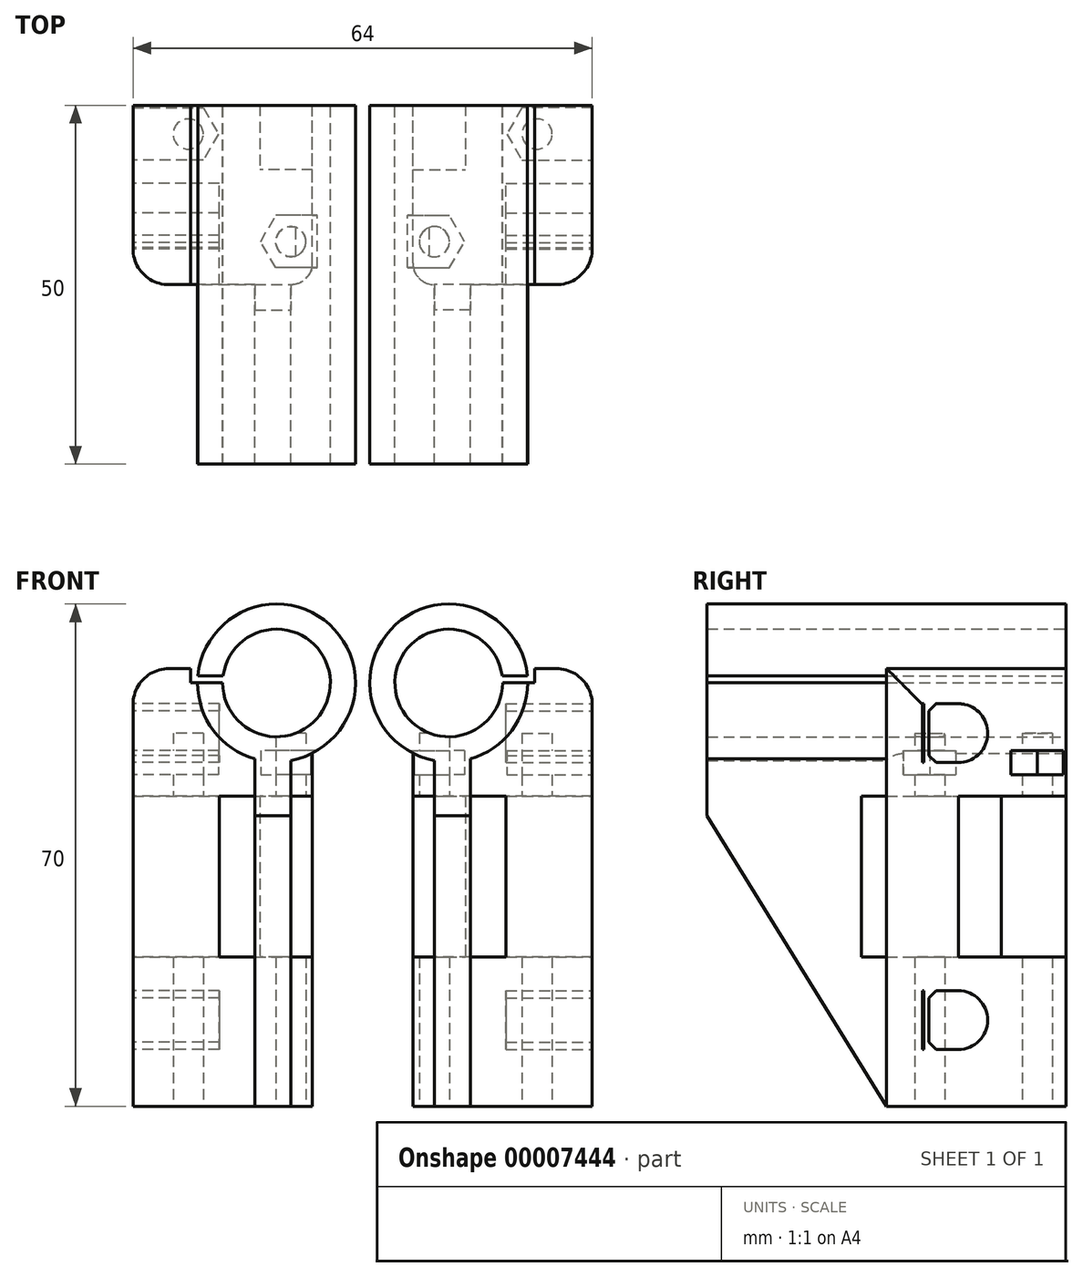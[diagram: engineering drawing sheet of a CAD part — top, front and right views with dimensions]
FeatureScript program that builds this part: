
annotation { "Feature Type Name" : "Feature", "Feature Type Description" : "" }
export const myFeature = defineFeature(function(context is Context, id is Id, definition is map)
    precondition{}
    {
        {
            var Q0;
            Q0=qCreatedBy(makeId("Front.planeOp"),FACE);
            var sketch = newSketch(context, id + "F0", { "sketchPlane" : qUnion([Q0])});
            skCircle(sketch, "E0", {"center": v(12, -12) * mm, "radius": 7.5 * mm});
            skCircle(sketch, "E1", {"center": v(12, -12) * mm, "radius": 11 * mm});
            skLineSegment(sketch, "E2", {"start": v(12, -12) * mm, "end": v(23, -12) * mm});
            skPoint(sketch, "E3.rect.middle", {"position": v(32, -10) * mm});
            skLineSegment(sketch, "E4", {"start": v(32, -10) * mm, "end": v(24, -10) * mm});
            skLineSegment(sketch, "E5", {"start": v(23, -12) * mm, "end": v(24, -12) * mm});
            skLineSegment(sketch, "E6", {"start": v(24, -12) * mm, "end": v(24, -10) * mm});
            skLineSegment(sketch, "E7", {"start": v(12, -12) * mm, "end": v(12, -11) * mm});
            skLineSegment(sketch, "E8", {"start": v(12, -11) * mm, "end": v(22.95, -11) * mm});
            skLineSegment(sketch, "E9", {"start": v(32, -10) * mm, "end": v(32, -71) * mm});
            skLineSegment(sketch, "E10", {"start": v(32, -71) * mm, "end": v(7, -71) * mm});
            skLineSegment(sketch, "E11", {"start": v(7, -71) * mm, "end": v(7, -23) * mm});
            skLineSegment(sketch, "E12", {"start": v(7, -23) * mm, "end": v(12, -23) * mm, "construction": true});
            skLineSegment(sketch, "E13", {"start": v(7, -23) * mm, "end": v(7, -21.8) * mm});
            skSolve(sketch);
        }
        {
            var Q0;
            {var subQ0=sQuery(id+"F0.wireOp",EDGE,"E2");var subQ1=sQuery(id+"F0.wireOp",EDGE,"E0");var subQ2=makeQuery(id+"F0.imprint","INTERSECT",VERTEX,{"derivedFrom":[subQ1,subQ0]});Q0=makeQuery(id+"F0.imprint","IMPRINT",FACE,{"disambiguationData":[TD([[makeQuery(id+"F0.imprint","IMPRINT",EDGE,{"disambiguationData":[TD([[subQ2,1.0]])],"derivedFrom":subQ1}),-1.0]])]});}
            extrude(context, id + "F1", {"entities" : qUnion([Q0]), "depth" : 50 * mm});
        }
        {
            var Q0;
            Q0=makeQuery(id+"F0.imprint","IMPRINT",FACE,{"disambiguationData":[TD([[makeQuery(id+"F0.imprint","IMPRINT",EDGE,{"derivedFrom":sQuery(id+"F0.wireOp",EDGE,"E4")}),1.0]])]});
            extrude(context, id + "F2", {"entities" : qUnion([Q0]), "operationType" : NewBodyOperationType.ADD, "depth" : 25 * mm});
        }
        {
            var Q0;
            Q0=makeQuery(id+"F2.opExtrude","SWEPT_FACE",FACE,{"disambiguationData":[OSD([sQuery(id+"F0.wireOp",EDGE,"E9")])]});
            var sketch = newSketch(context, id + "F3", { "sketchPlane" : qUnion([Q0])});
            skLineSegment(sketch, "E14", {"start": v(0, -71) * mm, "end": v(-15, -71) * mm, "construction": true});
            skLineSegment(sketch, "E15", {"start": v(-15, -71) * mm, "end": v(-15, -59) * mm, "construction": true});
            skLineSegment(sketch, "E16", {"start": v(-15, -59) * mm, "end": v(-15, -19) * mm, "construction": true});
            skCircle(sketch, "E17", {"center": v(-15, -59) * mm, "radius": 4.1 * mm});
            skCircle(sketch, "E18", {"center": v(-15, -59) * mm, "radius": 7.5 * mm, "construction": true});
            skCircle(sketch, "E19", {"center": v(-15, -19) * mm, "radius": 7.5 * mm, "construction": true});
            skLineSegment(sketch, "E20", {"start": v(-15, -39) * mm, "end": v(-16.5, -39) * mm, "construction": true});
            skLineSegment(sketch, "E21", {"start": v(-16.5, -39) * mm, "end": v(-16.5, -44.4) * mm, "construction": true});
            skCircle(sketch, "E22", {"center": v(-16.5, -44.4) * mm, "radius": 3 * mm, "construction": true});
            skCircle(sketch, "E23.0.MirrorC", {"center": v(-16.5, -33.6) * mm, "radius": 3 * mm, "construction": true});
            skLineSegment(sketch, "E24", {"start": v(-15, -54.9) * mm, "end": v(-20, -54.9) * mm, "construction": true});
            skLineSegment(sketch, "E25", {"start": v(-15, -63.1) * mm, "end": v(-20, -63.1) * mm, "construction": true});
            skLineSegment(sketch, "E26", {"start": v(-19.1, -54.9) * mm, "end": v(-19.1, -63.1) * mm});
            skLineSegment(sketch, "E27", {"start": v(-19.1, -55.9) * mm, "end": v(-18.1, -54.9) * mm});
            skLineSegment(sketch, "E28", {"start": v(-18.1, -54.9) * mm, "end": v(-15, -54.9) * mm});
            skLineSegment(sketch, "E29", {"start": v(-15, -63.1) * mm, "end": v(-18.1, -63.1) * mm});
            skLineSegment(sketch, "E30", {"start": v(-18.1, -63.1) * mm, "end": v(-19.1, -62.1) * mm});
            skLineSegment(sketch, "E31.bottom", {"start": v(-19.8, -54.9) * mm, "end": v(-20, -54.9) * mm});
            skLineSegment(sketch, "E31.top", {"start": v(-19.8, -63.1) * mm, "end": v(-20, -63.1) * mm});
            skLineSegment(sketch, "E31.left", {"start": v(-19.8, -54.9) * mm, "end": v(-19.8, -63.1) * mm});
            skLineSegment(sketch, "E31.right", {"start": v(-20, -54.9) * mm, "end": v(-20, -63.1) * mm});
            skLineSegment(sketch, "E32", {"start": v(-15, -39) * mm, "end": v(5.06, -39) * mm, "construction": true});
            skLineSegment(sketch, "E33.MirrorCS", {"start": v(-19.8, -23.1) * mm, "end": v(-20, -23.1) * mm});
            skLineSegment(sketch, "E34.MirrorCS", {"start": v(-19.8, -14.9) * mm, "end": v(-20, -14.9) * mm});
            skLineSegment(sketch, "E35.MirrorCS", {"start": v(-19.1, -22.1) * mm, "end": v(-18.1, -23.1) * mm});
            skLineSegment(sketch, "E36.MirrorCS", {"start": v(-18.1, -14.9) * mm, "end": v(-19.1, -15.9) * mm});
            skLineSegment(sketch, "E37.MirrorCS", {"start": v(-15, -14.9) * mm, "end": v(-20, -14.9) * mm, "construction": true});
            skLineSegment(sketch, "E38.MirrorCS", {"start": v(-15, -23.1) * mm, "end": v(-20, -23.1) * mm, "construction": true});
            skLineSegment(sketch, "E39.MirrorCS", {"start": v(-18.1, -23.1) * mm, "end": v(-15, -23.1) * mm});
            skLineSegment(sketch, "E40.MirrorCS", {"start": v(-19.8, -23.1) * mm, "end": v(-19.8, -14.9) * mm});
            skLineSegment(sketch, "E41.MirrorCS", {"start": v(-20, -23.1) * mm, "end": v(-20, -14.9) * mm});
            skLineSegment(sketch, "E42.MirrorCS", {"start": v(-19.1, -23.1) * mm, "end": v(-19.1, -14.9) * mm});
            skCircle(sketch, "E43.MirrorC", {"center": v(-15, -19) * mm, "radius": 4.1 * mm});
            skLineSegment(sketch, "E44.MirrorCS", {"start": v(-15, -14.9) * mm, "end": v(-18.1, -14.9) * mm});
            skSolve(sketch);
        }
        {
            var Q0;
            Q0=makeQuery(id+"F2.opExtrude","SWEPT_FACE",FACE,{"disambiguationData":[OSD([sQuery(id+"F0.wireOp",EDGE,"E10")])]});
            var sketch = newSketch(context, id + "F4", { "sketchPlane" : qUnion([Q0])});
            skLineSegment(sketch, "E45", {"start": v(0, 0) * mm, "end": v(0, 19) * mm, "construction": true});
            skLineSegment(sketch, "E46", {"start": v(0, 19) * mm, "end": v(10, 19) * mm, "construction": true});
            skLineSegment(sketch, "E47", {"start": v(10, 19) * mm, "end": v(10, 4) * mm, "construction": true});
            skLineSegment(sketch, "E48", {"start": v(10, 4) * mm, "end": v(24.3, 4) * mm, "construction": true});
            skCircle(sketch, "E49", {"center": v(10, 19) * mm, "radius": 2.1 * mm});
            skCircle(sketch, "E50", {"center": v(10, 19) * mm, "radius": 6.5 * mm, "construction": true});
            skCircle(sketch, "E51", {"center": v(24.3, 4) * mm, "radius": 2.1 * mm});
            skCircle(sketch, "E52", {"center": v(24.3, 4) * mm, "radius": 6.5 * mm, "construction": true});
            skLineSegment(sketch, "E53", {"start": v(14.3, 0) * mm, "end": v(14.3, 9) * mm});
            skLineSegment(sketch, "E54", {"start": v(20, 15) * mm, "end": v(32, 15) * mm});
            skLineSegment(sketch, "E55", {"start": v(32, 15) * mm, "end": v(32, 4) * mm});
            skLineSegment(sketch, "E56", {"start": v(24.3, 4) * mm, "end": v(24.3, 0) * mm, "construction": true});
            skLineSegment(sketch, "E57", {"start": v(24.3, 0) * mm, "end": v(14.3, 0) * mm});
            skLineSegment(sketch, "E58", {"start": v(20, 25) * mm, "end": v(20, 15) * mm});
            skLineSegment(sketch, "E59", {"start": v(7, 9) * mm, "end": v(14.3, 9) * mm});
            skLineSegment(sketch, "E60", {"start": v(7, 9) * mm, "end": v(7, 25) * mm});
            skLineSegment(sketch, "E61", {"start": v(7, 25) * mm, "end": v(20, 25) * mm});
            skLineSegment(sketch, "E62", {"start": v(24.3, 0) * mm, "end": v(32, 0) * mm});
            skLineSegment(sketch, "E63", {"start": v(32, 0) * mm, "end": v(32, 4) * mm});
            skLineSegment(sketch, "E64", {"start": v(32, 4) * mm, "end": v(24.3, 4) * mm, "construction": true});
            skSolve(sketch);
        }
        {
            var Q0;
            Q0=makeQuery(id+"F4.imprint","IMPRINT",FACE,{"disambiguationData":[TD([[makeQuery(id+"F4.imprint","IMPRINT",EDGE,{"derivedFrom":sQuery(id+"F4.wireOp",EDGE,"E49")}),-1.0]])]});
            extrude(context, id + "F5", {"entities" : qUnion([Q0]), "operationType" : NewBodyOperationType.REMOVE, "oppositeDirection" : true, "depth" : 12 * mm + (40 * mm + 22.4 * mm) * .5});
        }
        {
            var Q0;
            Q0=makeQuery(id+"F4.imprint","IMPRINT",FACE,{"disambiguationData":[TD([[makeQuery(id+"F4.imprint","IMPRINT",EDGE,{"derivedFrom":sQuery(id+"F4.wireOp",EDGE,"E49")}),-1.0]])]});
            extrude(context, id + "F6", {"entities" : qUnion([Q0]), "operationType" : NewBodyOperationType.ADD, "oppositeDirection" : true, "depth" : 12 * mm + (40 * mm - 22.4 * mm) * .5});
        }
        {
            var Q0;
            Q0=makeQuery(id+"F4.imprint","IMPRINT",FACE,{"disambiguationData":[TD([[makeQuery(id+"F4.imprint","IMPRINT",EDGE,{"derivedFrom":sQuery(id+"F4.wireOp",EDGE,"E49")}),1.0]])]});
            var Q1;
            Q1=makeQuery(id+"F4.imprint","IMPRINT",FACE,{"disambiguationData":[TD([[makeQuery(id+"F4.imprint","IMPRINT",EDGE,{"derivedFrom":sQuery(id+"F4.wireOp",EDGE,"E51")}),1.0]])]});
            extrude(context, id + "F7", {"entities" : qUnion([Q0, Q1]), "operationType" : NewBodyOperationType.REMOVE, "oppositeDirection" : true, "depth" : 12 * mm + 40 * mm});
        }
        {
            var Q0;
            Q0=makeQuery(id+"F5.boolean.opBoolean","COPY",FACE,{"derivedFrom":makeQuery(id+"F5.opExtrude","CAP_FACE",FACE,{"disambiguationData":[OSD([sQuery(id+"F4.wireOp",EDGE,"E49"),sQuery(id+"F4.wireOp",EDGE,"E51"),sQuery(id+"F4.wireOp",EDGE,"E53"),sQuery(id+"F4.wireOp",EDGE,"E54"),sQuery(id+"F4.wireOp",EDGE,"E55"),sQuery(id+"F4.wireOp",EDGE,"E57"),sQuery(id+"F4.wireOp",EDGE,"E58"),sQuery(id+"F4.wireOp",EDGE,"E59"),sQuery(id+"F4.wireOp",EDGE,"E60"),sQuery(id+"F4.wireOp",EDGE,"E61"),sQuery(id+"F4.wireOp",EDGE,"E62"),sQuery(id+"F4.wireOp",EDGE,"E63")])],"isStart":false})});
            var sketch = newSketch(context, id + "F8", { "sketchPlane" : qUnion([Q0])});
            skCircle(sketch, "E65.cCircle", {"center": v(24.3, 4) * mm, "radius": 3.65 * mm, "construction": true});
            skLineSegment(sketch, "E65.0", {"start": v(28.51, 4) * mm, "end": v(26.4, 0.35) * mm, "construction": true});
            skLineSegment(sketch, "E65.1", {"start": v(26.4, 0.35) * mm, "end": v(22.2, 0.35) * mm});
            skLineSegment(sketch, "E65.2", {"start": v(22.2, 0.35) * mm, "end": v(20.09, 4) * mm});
            skLineSegment(sketch, "E65.3", {"start": v(20.09, 4) * mm, "end": v(22.2, 7.65) * mm});
            skLineSegment(sketch, "E65.4", {"start": v(22.2, 7.65) * mm, "end": v(26.4, 7.65) * mm});
            skLineSegment(sketch, "E65.5", {"start": v(26.4, 7.65) * mm, "end": v(28.51, 4) * mm, "construction": true});
            skPoint(sketch, "E65.0.midPoint", {"position": v(27.46, 2.18) * mm});
            skCircle(sketch, "E66.cCircle", {"center": v(10, 19) * mm, "radius": 3.65 * mm, "construction": true});
            skLineSegment(sketch, "E66.0", {"start": v(14.21, 19) * mm, "end": v(12.1, 15.35) * mm});
            skLineSegment(sketch, "E66.1", {"start": v(12.1, 15.35) * mm, "end": v(7.9, 15.35) * mm});
            skLineSegment(sketch, "E66.2", {"start": v(7.9, 15.35) * mm, "end": v(5.79, 19) * mm, "construction": true});
            skLineSegment(sketch, "E66.3", {"start": v(5.79, 19) * mm, "end": v(7.9, 22.65) * mm, "construction": true});
            skLineSegment(sketch, "E66.4", {"start": v(7.9, 22.65) * mm, "end": v(12.1, 22.65) * mm});
            skLineSegment(sketch, "E66.5", {"start": v(12.1, 22.65) * mm, "end": v(14.21, 19) * mm});
            skPoint(sketch, "E66.0.midPoint", {"position": v(13.16, 17.18) * mm});
            skLineSegment(sketch, "E67", {"start": v(7.9, 22.65) * mm, "end": v(7, 22.65) * mm});
            skLineSegment(sketch, "E68", {"start": v(7, 22.65) * mm, "end": v(7, 15.35) * mm});
            skLineSegment(sketch, "E69", {"start": v(7, 15.35) * mm, "end": v(7.9, 15.35) * mm});
            skLineSegment(sketch, "E70", {"start": v(26.4, 7.65) * mm, "end": v(32, 7.65) * mm});
            skLineSegment(sketch, "E71", {"start": v(32, 7.65) * mm, "end": v(32, 0.35) * mm});
            skLineSegment(sketch, "E72", {"start": v(32, 0.35) * mm, "end": v(26.4, 0.35) * mm});
            skLineSegment(sketch, "E73", {"start": v(7, 22.65) * mm, "end": v(-3, 22.65) * mm});
            skLineSegment(sketch, "E74", {"start": v(-3, 22.65) * mm, "end": v(-3, 15.35) * mm});
            skLineSegment(sketch, "E75", {"start": v(-3, 15.35) * mm, "end": v(7, 15.35) * mm});
            skSolve(sketch);
        }
        {
            var Q0;
            Q0=makeQuery(id+"F8.imprint","IMPRINT",FACE,{"disambiguationData":[TD([[makeQuery(id+"F8.imprint","IMPRINT",EDGE,{"derivedFrom":sQuery(id+"F8.wireOp",EDGE,"E65.1")}),-1.0]])]});
            var Q1;
            Q1=makeQuery(id+"F8.imprint","IMPRINT",FACE,{"disambiguationData":[TD([[makeQuery(id+"F8.imprint","IMPRINT",EDGE,{"derivedFrom":sQuery(id+"F8.wireOp",EDGE,"E66.0")}),-1.0]])]});
            var Q2;
            Q2=makeQuery(id+"F8.imprint","IMPRINT",FACE,{"disambiguationData":[TD([[makeQuery(id+"F8.imprint","IMPRINT",EDGE,{"derivedFrom":sQuery(id+"F8.wireOp",EDGE,"E68")}),-1.0]])]});
            extrude(context, id + "F9", {"entities" : qUnion([Q0, Q1, Q2]), "operationType" : NewBodyOperationType.REMOVE, "oppositeDirection" : true, "depth" : 6.4 * mm});
        }
        {
            var Q0;
            Q0=makeQuery(id+"F8.imprint","IMPRINT",FACE,{"disambiguationData":[TD([[makeQuery(id+"F8.imprint","IMPRINT",EDGE,{"derivedFrom":sQuery(id+"F8.wireOp",EDGE,"E66.0")}),-1.0]])]});
            var Q1;
            Q1=makeQuery(id+"F8.imprint","IMPRINT",FACE,{"disambiguationData":[TD([[makeQuery(id+"F8.imprint","IMPRINT",EDGE,{"derivedFrom":sQuery(id+"F8.wireOp",EDGE,"E65.1")}),-1.0]])]});
            extrude(context, id + "F10", {"entities" : qUnion([Q0, Q1]), "operationType" : NewBodyOperationType.ADD, "oppositeDirection" : true, "depth" : 3 * mm});
        }
        {
            var Q0;
            Q0 = qSketchRegion(id + "F3", true);
            extrude(context, id + "F11", {"entities" : qUnion([Q0]), "operationType" : NewBodyOperationType.REMOVE, "oppositeDirection" : true, "depth" : 12 * mm});
        }
        {
            var Q0;
            Q0=makeQuery(id+"F10.boolean.opBoolean","MERGE",FACE,{"derivedFrom":[makeQuery(id+"F6.boolean.opBoolean","MERGE",FACE,{"derivedFrom":[makeQuery(id+"F2.opExtrude","SWEPT_FACE",FACE,{"disambiguationData":[OSD([sQuery(id+"F0.wireOp",EDGE,"E11"),sQuery(id+"F0.wireOp",EDGE,"E13")])]}),makeQuery(id+"F6.opExtrude","SWEPT_FACE",FACE,{"disambiguationData":[OSD([sQuery(id+"F4.wireOp",EDGE,"E60")])]})]}),makeQuery(id+"F10.opExtrude","SWEPT_FACE",FACE,{"disambiguationData":[OSD([sQuery(id+"F8.wireOp",EDGE,"E68")])]})]});
            cPlane(context, id + "F12", {"entities" : qUnion([Q0]), "cplaneType" : CPlaneType.OFFSET, "offset" : 3 * mm, "oppositeDirection" : true, "width" : 150 * mm, "height" : 150 * mm});
        }
        {
            var Q0;
            Q0=qCreatedBy(id+"F12.planeOp",FACE);
            var sketch = newSketch(context, id + "F13", { "sketchPlane" : qUnion([Q0])});
            skLineSegment(sketch, "E76.0.0", {"start": v(9, -50.2) * mm, "end": v(9, -27.8) * mm});
            skLineSegment(sketch, "E76.0.1", {"start": v(9, -27.8) * mm, "end": v(25, -27.8) * mm});
            skLineSegment(sketch, "E76.0.2", {"start": v(25, -27.8) * mm, "end": v(25, -21.8) * mm});
            skLineSegment(sketch, "E76.0.4", {"start": v(0, -21.8) * mm, "end": v(0, -71) * mm});
            skLineSegment(sketch, "E76.0.5", {"start": v(0, -71) * mm, "end": v(25, -71) * mm});
            skLineSegment(sketch, "E76.0.6", {"start": v(25, -71) * mm, "end": v(25, -50.2) * mm});
            skLineSegment(sketch, "E76.0.7", {"start": v(25, -50.2) * mm, "end": v(9, -50.2) * mm});
            skLineSegment(sketch, "E77", {"start": v(25, -27.8) * mm, "end": v(28.5, -27.8) * mm});
            skLineSegment(sketch, "E78", {"start": v(28.5, -27.8) * mm, "end": v(28.5, -50.2) * mm});
            skLineSegment(sketch, "E79", {"start": v(28.5, -50.2) * mm, "end": v(25, -50.2) * mm});
            skLineSegment(sketch, "E80.0", {"start": v(50, -1) * mm, "end": v(50, -23) * mm});
            skLineSegment(sketch, "E81", {"start": v(25, -20.5) * mm, "end": v(25, -21.8) * mm});
            skLineSegment(sketch, "E82", {"start": v(25, -20.5) * mm, "end": v(50, -20.5) * mm});
            skLineSegment(sketch, "E83", {"start": v(50, -20.5) * mm, "end": v(50, -30.5) * mm});
            skLineSegment(sketch, "E84", {"start": v(50, -30.5) * mm, "end": v(25, -71) * mm});
            skLineSegment(sketch, "E85", {"start": v(43, -29) * mm, "end": v(43, -38.5) * mm, "construction": true});
            skCircle(sketch, "E86", {"center": v(43, -29) * mm, "radius": 1.05 * mm, "construction": true});
            skCircle(sketch, "E87", {"center": v(43, -38.5) * mm, "radius": 1.05 * mm, "construction": true});
            skPoint(sketch, "E88.0", {"position": v(0, -12) * mm});
            skSolve(sketch);
        }
        {
            var Q0;
            Q0=makeQuery(id+"F13.imprint","IMPRINT",FACE,{"disambiguationData":[TD([[makeQuery(id+"F13.imprint","IMPRINT",EDGE,{"derivedFrom":sQuery(id+"F13.wireOp",EDGE,"E76.0.2")}),-1.0]])]});
            extrude(context, id + "F14", {"entities" : qUnion([Q0]), "operationType" : NewBodyOperationType.ADD, "oppositeDirection" : true, "depth" : 5 * mm});
        }
        {
            var Q0;
            {var subQ0=sQuery(id+"F0.wireOp",EDGE,"E1");var subQ1=sQuery(id+"F0.wireOp",EDGE,"E4");var subQ2=sQuery(id+"F0.wireOp",EDGE,"E5");var subQ3=sQuery(id+"F0.wireOp",EDGE,"E6");var subQ4=sQuery(id+"F0.wireOp",EDGE,"E9");var subQ5=sQuery(id+"F0.wireOp",EDGE,"E10");var subQ6=sQuery(id+"F4.wireOp",EDGE,"E61");var subQ7=sQuery(id+"F13.wireOp",EDGE,"E77");var subQ8=sQuery(id+"F8.wireOp",EDGE,"E71");var subQ9=sQuery(id+"F4.wireOp",EDGE,"E49");var subQ10=sQuery(id+"F4.wireOp",EDGE,"E51");var subQ11=sQuery(id+"F13.wireOp",EDGE,"E79");var subQ12=sQuery(id+"F13.wireOp",EDGE,"E84");var subQ13=sQuery(id+"F4.wireOp",EDGE,"E53");var subQ14=sQuery(id+"F4.wireOp",EDGE,"E54");var subQ15=sQuery(id+"F4.wireOp",EDGE,"E55");var subQ16=sQuery(id+"F4.wireOp",EDGE,"E57");var subQ17=sQuery(id+"F4.wireOp",EDGE,"E58");var subQ18=sQuery(id+"F4.wireOp",EDGE,"E59");var subQ19=sQuery(id+"F4.wireOp",EDGE,"E60");var subQ20=sQuery(id+"F4.wireOp",EDGE,"E62");var subQ21=sQuery(id+"F4.wireOp",EDGE,"E63");Q0=makeQuery(id+"F14.boolean.opBoolean","SPLIT",FACE,{"disambiguationData":[TD([makeQuery(id+"F1.opExtrude","SWEPT_FACE",FACE,{"disambiguationData":[OSD([subQ0])]}),makeQuery(id+"F1.opExtrude","SWEPT_FACE",FACE,{"disambiguationData":[OSD([sQuery(id+"F0.wireOp",EDGE,"E2")])]}),makeQuery(id+"F2.opExtrude","SWEPT_FACE",FACE,{"disambiguationData":[OSD([subQ1])]}),makeQuery(id+"F2.opExtrude","SWEPT_FACE",FACE,{"disambiguationData":[OSD([subQ2])]}),makeQuery(id+"F2.opExtrude","SWEPT_FACE",FACE,{"disambiguationData":[OSD([subQ3])]}),makeQuery(id+"F2.opExtrude","SWEPT_FACE",FACE,{"disambiguationData":[OSD([subQ4])]}),makeQuery(id+"F2.opExtrude","SWEPT_FACE",FACE,{"disambiguationData":[OSD([subQ5])]}),makeQuery(id+"F5.boolean.opBoolean","COPY",FACE,{"derivedFrom":makeQuery(id+"F5.opExtrude","CAP_FACE",FACE,{"disambiguationData":[OSD([subQ9,subQ10,subQ13,subQ14,subQ15,subQ16,subQ17,subQ18,subQ19,subQ6,subQ20,subQ21])],"isStart":false})}),makeQuery(id+"F5.boolean.opBoolean","COPY",FACE,{"derivedFrom":makeQuery(id+"F5.opExtrude","SWEPT_FACE",FACE,{"disambiguationData":[OSD([subQ17])]})}),makeQuery(id+"F6.opExtrude","CAP_FACE",FACE,{"disambiguationData":[OSD([subQ9,subQ10,subQ13,subQ14,subQ15,subQ16,subQ17,subQ18,subQ19,subQ6,subQ20,subQ21])],"isStart":true}),makeQuery(id+"F6.opExtrude","CAP_FACE",FACE,{"disambiguationData":[OSD([subQ9,subQ10,subQ13,subQ14,subQ15,subQ16,subQ17,subQ18,subQ19,subQ6,subQ20,subQ21])],"isStart":false}),makeQuery(id+"F6.opExtrude","SWEPT_FACE",FACE,{"disambiguationData":[OSD([subQ15,subQ21])]}),makeQuery(id+"F10.opExtrude","CAP_FACE",FACE,{"disambiguationData":[OSD([subQ10,sQuery(id+"F8.wireOp",EDGE,"E65.1"),sQuery(id+"F8.wireOp",EDGE,"E65.2"),sQuery(id+"F8.wireOp",EDGE,"E65.3"),sQuery(id+"F8.wireOp",EDGE,"E65.4"),sQuery(id+"F8.wireOp",EDGE,"E70"),subQ8,sQuery(id+"F8.wireOp",EDGE,"E72")])],"isStart":true}),makeQuery(id+"F10.opExtrude","CAP_FACE",FACE,{"disambiguationData":[OSD([subQ9,sQuery(id+"F8.wireOp",EDGE,"E66.0"),sQuery(id+"F8.wireOp",EDGE,"E66.1"),sQuery(id+"F8.wireOp",EDGE,"E66.4"),sQuery(id+"F8.wireOp",EDGE,"E66.5"),sQuery(id+"F8.wireOp",EDGE,"E67"),sQuery(id+"F8.wireOp",EDGE,"E68"),sQuery(id+"F8.wireOp",EDGE,"E69")])],"isStart":true}),makeQuery(id+"F10.opExtrude","SWEPT_FACE",FACE,{"disambiguationData":[OSD([subQ8])]}),makeQuery(id+"F14.opExtrude","CAP_FACE",FACE,{"disambiguationData":[OSD([sQuery(id+"F13.wireOp",EDGE,"E76.0.2"),sQuery(id+"F13.wireOp",EDGE,"E76.0.6"),subQ7,sQuery(id+"F13.wireOp",EDGE,"E78"),subQ11,sQuery(id+"F13.wireOp",EDGE,"E82"),sQuery(id+"F13.wireOp",EDGE,"E83"),subQ12,sQuery(id+"F13.wireOp",EDGE,"E86"),sQuery(id+"F13.wireOp",EDGE,"E87")])],"isStart":false}),makeQuery(id+"F14.opExtrude","SWEPT_FACE",FACE,{"disambiguationData":[OSD([subQ7])]}),makeQuery(id+"F14.opExtrude","SWEPT_FACE",FACE,{"disambiguationData":[OSD([subQ11])]}),makeQuery(id+"F14.opExtrude","SWEPT_FACE",FACE,{"disambiguationData":[OSD([subQ12])]})])],"derivedFrom":makeQuery(id+"F6.boolean.opBoolean","MERGE",FACE,{"derivedFrom":[makeQuery(id+"F2.opExtrude","CAP_FACE",FACE,{"disambiguationData":[OSD([subQ0,subQ1,subQ2,subQ3,subQ4,subQ5,sQuery(id+"F0.wireOp",EDGE,"E11"),sQuery(id+"F0.wireOp",EDGE,"E13")])],"isStart":false}),makeQuery(id+"F6.opExtrude","SWEPT_FACE",FACE,{"disambiguationData":[OSD([subQ6])]})]})});}
            var sketch = newSketch(context, id + "F15", { "sketchPlane" : qUnion([Q0])});
            skLineSegment(sketch, "E89", {"start": v(25, -28) * mm, "end": v(25, -37.5) * mm, "construction": true});
            skCircle(sketch, "E90", {"center": v(25, -37.5) * mm, "radius": 1.05 * mm});
            skCircle(sketch, "E91", {"center": v(25, -28) * mm, "radius": 1.05 * mm});
            skSolve(sketch);
        }
        {
            var Q0;
            Q0=qCreatedBy(makeId("Right.planeOp"),FACE);
            var Q1;
            Q1=sQuery(id+"F0.wireOp",VERTEX,"E1.center");
            cPlane(context, id + "F16", {"entities" : qUnion([Q0, Q1]), "cplaneType" : CPlaneType.PLANE_POINT, "offset" : 150 * mm, "width" : 150 * mm, "height" : 150 * mm});
        }
        {
            var Q0;
            Q0=qCreatedBy(id+"F16.planeOp",FACE);
            var sketch = newSketch(context, id + "F17", { "sketchPlane" : qUnion([Q0])});
            skPoint(sketch, "E92.0", {"position": v(0, -12) * mm});
            skLineSegment(sketch, "E93.0", {"start": v(0, -19.5) * mm, "end": v(0, -4.5) * mm});
            skLineSegment(sketch, "E94.0", {"start": v(-50, -19.5) * mm, "end": v(-50, -4.5) * mm});
            skLineSegment(sketch, "E95", {"start": v(0, -12) * mm, "end": v(-50, -12) * mm});
            skArc(sketch, "E96", {"start": v(-2, -19.27) * mm, "mid": v(-10, -18) * mm, "end": v(-18, -19.27) * mm});
            skLineSegment(sketch, "E97", {"start": v(-2, -4.73) * mm, "end": v(-18, -4.73) * mm, "construction": true});
            skLineSegment(sketch, "E98", {"start": v(-2, -19.27) * mm, "end": v(0.34, -20.03) * mm, "construction": true});
            skLineSegment(sketch, "E99", {"start": v(-10, -43.89) * mm, "end": v(-10, -12) * mm, "construction": true});
            skArc(sketch, "E100", {"start": v(-2, -19.27) * mm, "mid": v(-0.85, -12) * mm, "end": v(-2, -4.73) * mm});
            skArc(sketch, "E101", {"start": v(-18, -4.73) * mm, "mid": v(-19.15, -12) * mm, "end": v(-18, -19.27) * mm});
            skLineSegment(sketch, "E102", {"start": v(-2, -19.27) * mm, "end": v(-2.8, -21.7) * mm, "construction": true});
            skPoint(sketch, "E103", {"position": v(-10, -18) * mm});
            skLineSegment(sketch, "E104", {"start": v(-25, -12) * mm, "end": v(-25, -25.7) * mm, "construction": true});
            skArc(sketch, "E105.0.MirrorCS", {"start": v(-32, -4.73) * mm, "mid": v(-30.85, -12) * mm, "end": v(-32, -19.27) * mm});
            skArc(sketch, "E105.1.MirrorCS", {"start": v(-48, -19.27) * mm, "mid": v(-40, -18) * mm, "end": v(-32, -19.27) * mm});
            skArc(sketch, "E105.2.MirrorCS", {"start": v(-48, -19.27) * mm, "mid": v(-49.15, -12) * mm, "end": v(-48, -4.73) * mm});
            skSolve(sketch);
        }
        {
            var Q0;
            Q0=makeQuery(id+"F2.opExtrude","CAP_EDGE",EDGE,{"disambiguationData":[OSD([sQuery(id+"F0.wireOp",EDGE,"E9")])],"isStart":false});
            var Q1;
            Q1=makeQuery(id+"F2.opExtrude","SWEPT_EDGE",EDGE,{"disambiguationData":[OSD([sQuery(id+"F0.wireOp",EDGE,"E4"),sQuery(id+"F0.wireOp",EDGE,"E9")])]});
            fillet(context, id + "F18", {"entities" : qUnion([Q0, Q1]), "radius" : 5 * mm, "tangentPropagation" : true, "allowEdgeOverflow" : false});
        }
        {
            var Q0;
            Q0=makeQuery(id+"F2.opExtrude","CAP_EDGE",EDGE,{"disambiguationData":[OSD([sQuery(id+"F0.wireOp",EDGE,"E11"),sQuery(id+"F0.wireOp",EDGE,"E13")])],"isStart":false});
            var Q1;
            Q1=makeQuery(id+"F6.opExtrude","SWEPT_EDGE",EDGE,{"disambiguationData":[OSD([sQuery(id+"F4.wireOp",EDGE,"E60"),sQuery(id+"F4.wireOp",EDGE,"E61")])]});
            fillet(context, id + "F19", {"entities" : qUnion([Q0, Q1]), "radius" : 3 * mm, "tangentPropagation" : true, "allowEdgeOverflow" : false});
        }
        {
            var Q0;
            Q0=makeQuery(id+"F1.opExtrude","SWEPT_BODY",BODY,{"disambiguationData":[OSD([sQuery(id+"F0.wireOp",EDGE,"E0"),sQuery(id+"F0.wireOp",EDGE,"E1"),sQuery(id+"F0.wireOp",EDGE,"E2"),sQuery(id+"F0.wireOp",EDGE,"E8")])]});
            var Q1;
            Q1=qCreatedBy(makeId("Right.planeOp"),FACE);
            mirror(context, id + "F20", {"entities" : qUnion([Q0]), "mirrorPlane" : qUnion([Q1])});
        }
    });
